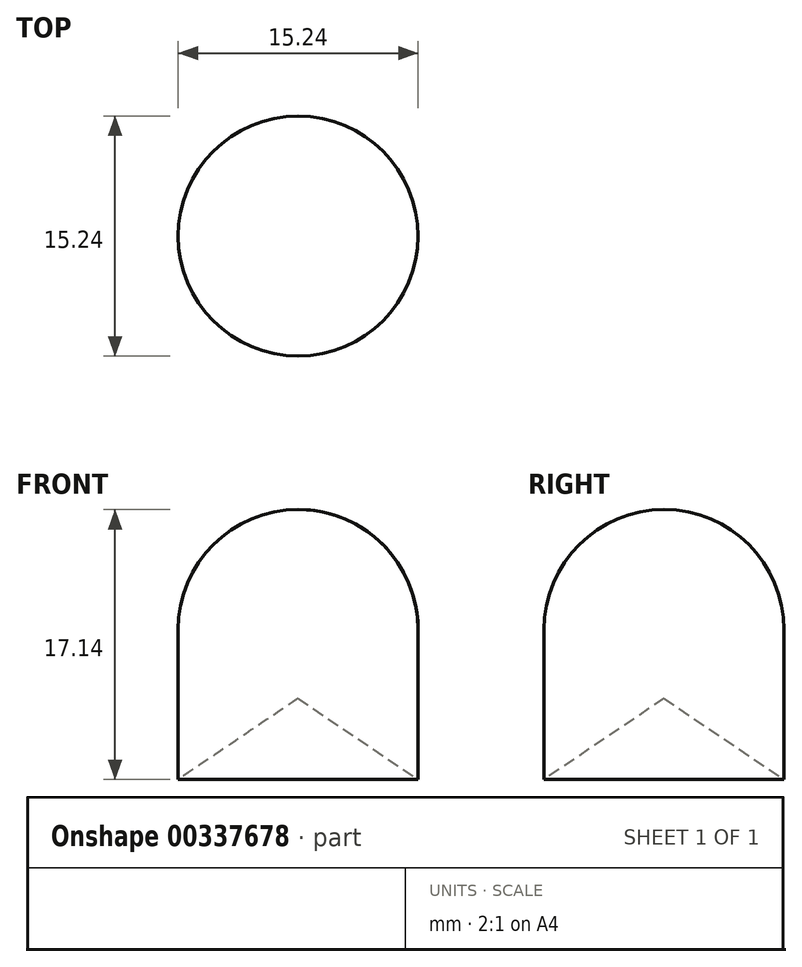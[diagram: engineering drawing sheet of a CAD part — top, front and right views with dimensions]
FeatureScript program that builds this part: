
annotation { "Feature Type Name" : "Feature", "Feature Type Description" : "" }
export const myFeature = defineFeature(function(context is Context, id is Id, definition is map)
    precondition{}
    {
        {
            var Q0;
            Q0=qCreatedBy(makeId("Front.planeOp"),FACE);
            var sketch = newSketch(context, id + "F0", { "sketchPlane" : qUnion([Q0])});
            skLineSegment(sketch, "E0", {"start": v(-7.62, -5.14) * mm, "end": v(-7.62, 4.38) * mm});
            skArc(sketch, "E1", {"start": v(-7.62, 4.38) * mm, "mid": v(-5.39, 9.77) * mm, "end": v(0, 12) * mm});
            skLineSegment(sketch, "E2", {"start": v(0, 12) * mm, "end": v(0, -5.14) * mm});
            skLineSegment(sketch, "E3", {"start": v(0, -5.14) * mm, "end": v(-7.62, -5.14) * mm});
            skLineSegment(sketch, "E4", {"start": v(0, 21.2) * mm, "end": v(0, -17.88) * mm});
            skSolve(sketch);
        }
        {
            var Q0;
            Q0=makeQuery(id+"F0.imprint","IMPRINT",FACE,{"disambiguationData":[TD([[makeQuery(id+"F0.imprint","IMPRINT",EDGE,{"derivedFrom":sQuery(id+"F0.wireOp",EDGE,"E0")}),-1.0]])]});
            var Q1;
            Q1=sQuery(id+"F0.wireOp",EDGE,"E2");
            revolve(context, id + "F1", {"entities" : qUnion([Q0]), "axis" : qUnion([Q1]), "revolveType" : RevolveType.FULL});
        }
        {
            var Q1;
            Q1=makeQuery(id+"F1.opRevolve","SWEPT_FACE",FACE,{"disambiguationData":[OSD([sQuery(id+"F0.wireOp",EDGE,"E3")])]});
            var Q2;
            Q2=qCreatedBy(makeId("Origin.pointOp"),VERTEX);
            loft(context, id + "F2", {"operationType" : NewBodyOperationType.REMOVE, "sheetProfilesArray" : [{ "sheetProfileEntities" : qUnion([Q1]) }, { "sheetProfileEntities" : qUnion([Q2]) }]});
        }
    });
